# Revit family: INGROUND 2W SIMETRICA_LKB0116WW.30
name_source: partatom
category: Luminarias
units: mm (PartAtom-declared; Revit-internal decimal feet)

## family parameters
Compartido = No
Corte con vacíos al cargar = No
Cota de conector redondo = Diámetro de uso
Origen de luz = Sí
Punto de cálculo de habitación = No
Se basa en plano de trabajo = Sí
Siempre vertical = No
Tipo de pieza = Normal

## types (2) — shared parameters
Cambio de temperatura de color de luz atenuada = <Ninguno>
Fabricante = BRILLANT
Filtro de color = 16777215
Watt per fixture = 3
Ángulo de campo de foco = 30.00°
Ángulo de enfoque = 30.00°
Ángulo de inclinación = 30.00°
zero-valued in all types: Elevación por defecto

## per-type parameters (varying)
| type | Comentarios de vataje | Descripción | Longitud de símbolo de origen de luz | Lámpara | Modelo |
| SUB_LKSC01WW.30 | 24 | LUMINARIA SUB ACUATICA TIPO PUNTUAL PARA EMPOTRAR EN PISO 68.5MM DE DIAMETRO POR 135MM DE ALTO CONSIDERANDO EL HOUSING, ACABADO EN ACERO INOXIDABLE, CUERPO MOLDEADO EN CROMO, SELLO DE SILICON, VIDRIO TEMPLADO DE 7MM, 1 LED TIPO OSRAM CON UN CONSUMO TOTAL DE 3 W, 115 LUMENES, CON UNA TEMPERATURA EN BLANCO CALIDO 3000K , IP 68, IK 08, SUMERGIBLE MAXIMO 2M, CABLE H07RN DE 3M, APERTURA EN STOCK A 30 GRADOS, ALIMENTADA A 24V. REQUIERE ACCESORIOS. | 3048 mm  [stored 10 ft] | Osram | LKSC01WW.30 |
| EMP_LKB0116WW.30 | 100-240V | LUMINARIA TIPO CIRCULAR PARA EMPOTRAR EN PISO CON CUERPO DE ALUMINIO FUNDIDO A PRESION CUBIERTO CON POLVO GRIS OSCURO, CON CUBIERTA DE ACERO INOXIDABLE Y VIDRIO TEMPLADO DE 7MM, HOUSING TIPO ABS DE 48MM DE DIAMETRO Y 98MM DE PROFUNDO. CUENTA CON 1 LED OSRAM CON UNA POTENCIA TOTAL DE 3W, A UNA TEMPERATURA EN BLANCO CALIDO DE 3000K CON 143 LUMENES, 47mA EN CORRIENTE DE OPERACIÓN, IP67, IK08, IRC 80, DISPONIBLE PARA ATENUAR EN TRIAC (OPCIONAL), APERTURA EN 30 GRADOS EN STOCK, ALIMENTADA A 100-240V | 500 mm  [stored 1.64042 ft] | OSRAM | LKB0116WW.30 |

note: [stored X ft] marks values corroborated as IEEE doubles in the binary element streams (Revit-internal decimal feet)

## geometry (parser evidence)
native form markers: Blend x2
no freeform markers — native parametric forms only
